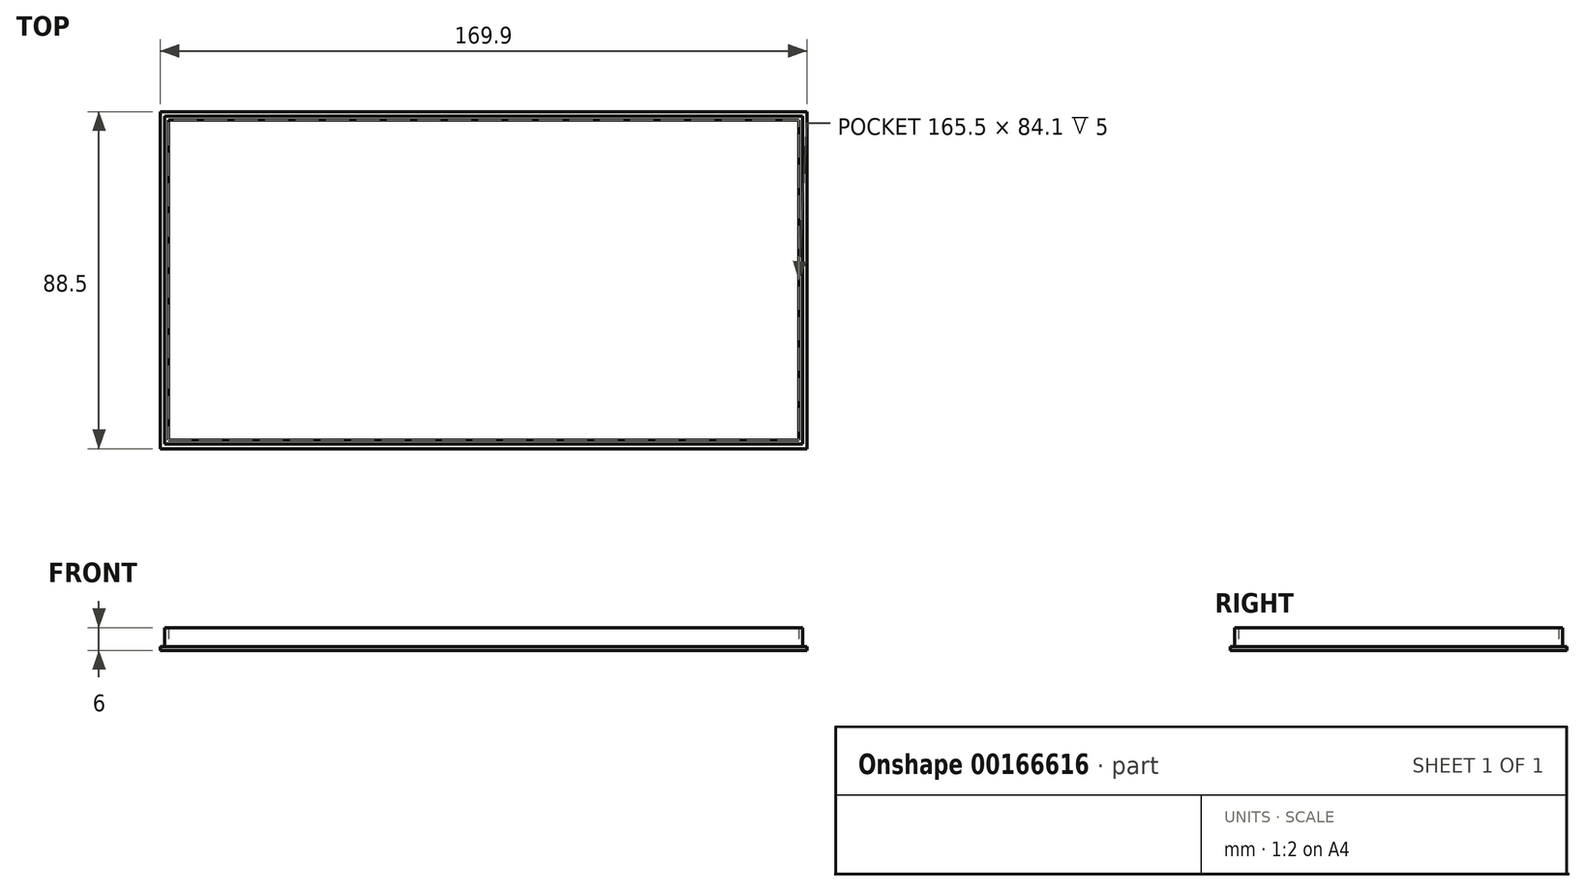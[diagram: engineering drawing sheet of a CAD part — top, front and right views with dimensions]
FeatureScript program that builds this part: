
annotation { "Feature Type Name" : "Feature", "Feature Type Description" : "" }
export const myFeature = defineFeature(function(context is Context, id is Id, definition is map)
    precondition{}
    {
        {
            var Q0;
            Q0=qCreatedBy(makeId("Top.planeOp"),FACE);
            var sketch = newSketch(context, id + "F0", { "sketchPlane" : qUnion([Q0])});
            skLineSegment(sketch, "E0.bottom", {"start": v(-87.35, 51.31) * mm, "end": v(82.55, 51.31) * mm});
            skLineSegment(sketch, "E0.top", {"start": v(-87.35, -37.19) * mm, "end": v(82.55, -37.19) * mm});
            skLineSegment(sketch, "E0.left", {"start": v(-87.35, 51.31) * mm, "end": v(-87.35, -37.19) * mm});
            skLineSegment(sketch, "E0.right", {"start": v(82.55, 51.31) * mm, "end": v(82.55, -37.19) * mm});
            skSolve(sketch);
        }
        {
            var Q0;
            Q0 = qSketchRegion(id + "F0", true);
            extrude(context, id + "F1", {"entities" : qUnion([Q0]), "depth" : 1 * mm});
        }
        {
            var Q0;
            Q0=makeQuery(id+"F1.opExtrude","CAP_FACE",FACE,{"disambiguationData":[OSD([sQuery(id+"F0.wireOp",EDGE,"E0.bottom"),sQuery(id+"F0.wireOp",EDGE,"E0.top"),sQuery(id+"F0.wireOp",EDGE,"E0.left"),sQuery(id+"F0.wireOp",EDGE,"E0.right")])],"isStart":false});
            var sketch = newSketch(context, id + "F2", { "sketchPlane" : qUnion([Q0])});
            skLineSegment(sketch, "E1.0", {"start": v(-87.35, 51.31) * mm, "end": v(82.55, 51.31) * mm});
            skLineSegment(sketch, "E2.0", {"start": v(82.55, 51.31) * mm, "end": v(82.55, -37.19) * mm});
            skLineSegment(sketch, "E3.0", {"start": v(-87.35, -37.19) * mm, "end": v(82.55, -37.19) * mm});
            skLineSegment(sketch, "E4.0", {"start": v(-87.35, 51.31) * mm, "end": v(-87.35, -37.19) * mm});
            skLineSegment(sketch, "E5.0", {"start": v(-86.15, 50.11) * mm, "end": v(81.35, 50.11) * mm});
            skLineSegment(sketch, "E5.1", {"start": v(-86.15, 50.11) * mm, "end": v(-86.15, -35.99) * mm});
            skLineSegment(sketch, "E5.2", {"start": v(-86.15, -35.99) * mm, "end": v(81.35, -35.99) * mm});
            skLineSegment(sketch, "E5.3", {"start": v(81.35, 50.11) * mm, "end": v(81.35, -35.99) * mm});
            skLineSegment(sketch, "E6.0", {"start": v(-85.15, 49.11) * mm, "end": v(80.35, 49.11) * mm});
            skLineSegment(sketch, "E6.1", {"start": v(-85.15, 49.11) * mm, "end": v(-85.15, -34.99) * mm});
            skLineSegment(sketch, "E6.2", {"start": v(-85.15, -34.99) * mm, "end": v(80.35, -34.99) * mm});
            skLineSegment(sketch, "E6.3", {"start": v(80.35, 49.11) * mm, "end": v(80.35, -34.99) * mm});
            skSolve(sketch);
        }
        {
            var Q0;
            Q0=makeQuery(id+"F2.imprint","IMPRINT",FACE,{"disambiguationData":[TD([[makeQuery(id+"F2.imprint","IMPRINT",EDGE,{"derivedFrom":sQuery(id+"F2.wireOp",EDGE,"E5.0")}),-1.0]])]});
            extrude(context, id + "F3", {"entities" : qUnion([Q0]), "operationType" : NewBodyOperationType.ADD, "depth" : 5 * mm});
        }
    });
